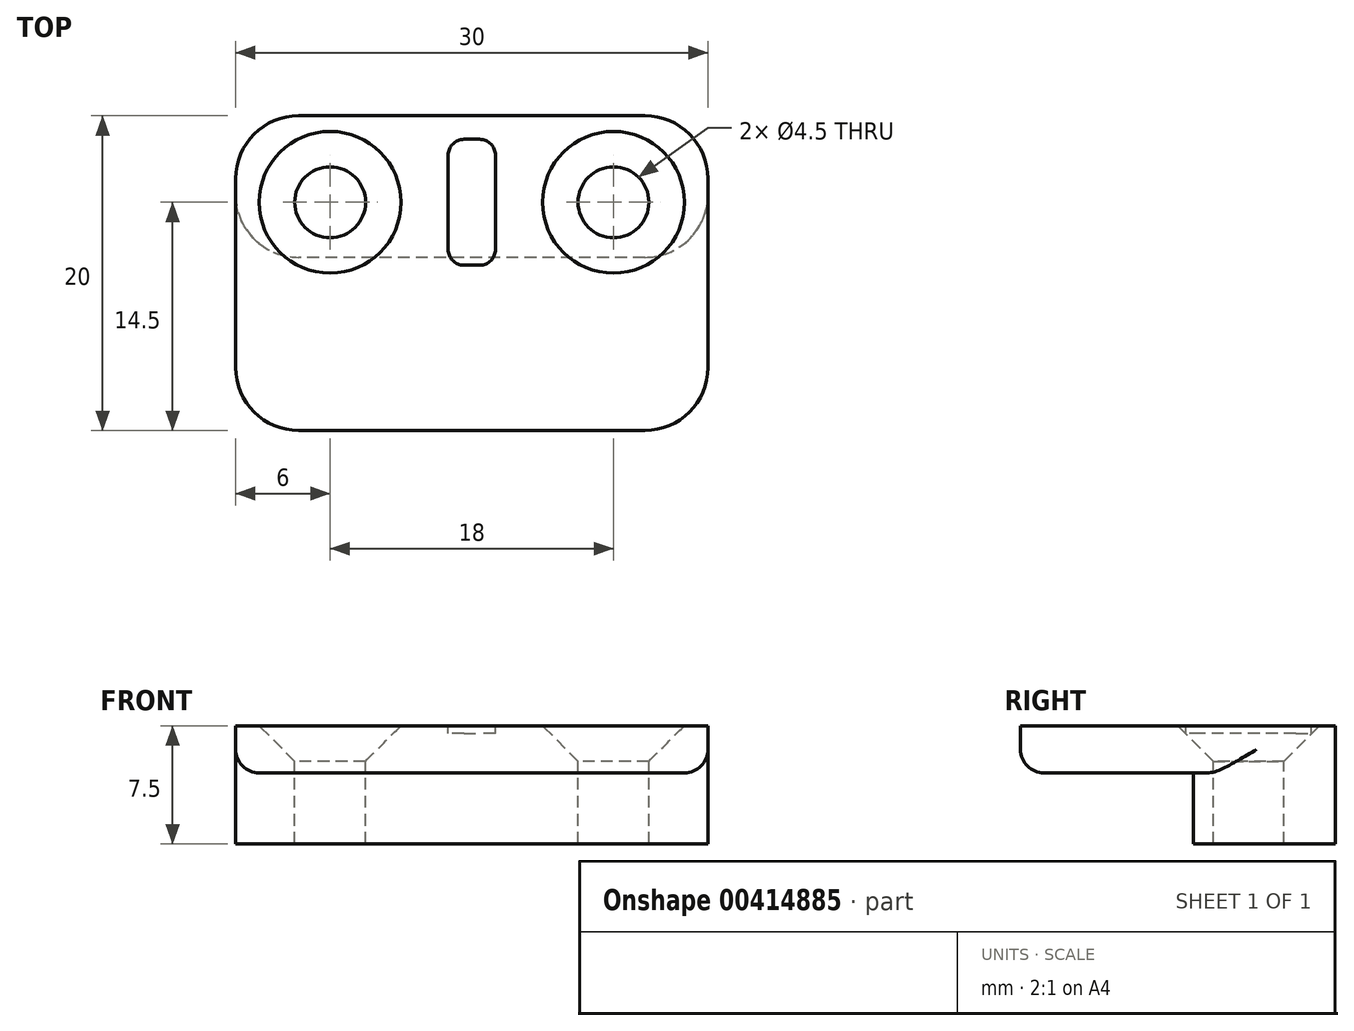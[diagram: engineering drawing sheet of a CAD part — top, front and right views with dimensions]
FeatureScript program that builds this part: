
annotation { "Feature Type Name" : "Feature", "Feature Type Description" : "" }
export const myFeature = defineFeature(function(context is Context, id is Id, definition is map)
    precondition{}
    {
        {
            var Q0;
            Q0=qCreatedBy(makeId("Right.planeOp"),FACE);
            var sketch = newSketch(context, id + "F0", { "sketchPlane" : qUnion([Q0])});
            skLineSegment(sketch, "E0", {"start": v(0, 0) * mm, "end": v(0, 4.5) * mm});
            skLineSegment(sketch, "E1", {"start": v(0, 4.5) * mm, "end": v(-11, 4.5) * mm});
            skLineSegment(sketch, "E2", {"start": v(-11, 4.5) * mm, "end": v(-11, 7.5) * mm});
            skLineSegment(sketch, "E3", {"start": v(-11, 7.5) * mm, "end": v(9, 7.5) * mm});
            skLineSegment(sketch, "E4", {"start": v(9, 7.5) * mm, "end": v(9, 0) * mm});
            skLineSegment(sketch, "E5", {"start": v(9, 0) * mm, "end": v(0, 0) * mm});
            skSolve(sketch);
        }
        {
            var Q0;
            Q0=makeQuery(id+"F0.imprint","IMPRINT",FACE,{"disambiguationData":[TD([[makeQuery(id+"F0.imprint","IMPRINT",EDGE,{"derivedFrom":sQuery(id+"F0.wireOp",EDGE,"E0")}),-1.0]])]});
            extrude(context, id + "F1", {"entities" : qUnion([Q0]), "endBound" : BoundingType.SYMMETRIC, "depth" : 30 * mm});
        }
        {
            var Q0;
            Q0=makeQuery(id+"F1.opExtrude","SWEPT_FACE",FACE,{"disambiguationData":[OSD([sQuery(id+"F0.wireOp",EDGE,"E3")])]});
            var sketch = newSketch(context, id + "F2", { "sketchPlane" : qUnion([Q0])});
            skLineSegment(sketch, "E6", {"start": v(-9, 3.5) * mm, "end": v(9, 3.5) * mm, "construction": true});
            skPoint(sketch, "E7.0", {"position": v(0, -11) * mm});
            skLineSegment(sketch, "E8", {"start": v(0, -11) * mm, "end": v(0, 3.5) * mm, "construction": true});
            skSolve(sketch);
        }
        {
            var Q0;
            Q0=sQuery(id+"F2.wireOp",VERTEX,"E6.start");
            var Q1;
            Q1=sQuery(id+"F2.wireOp",VERTEX,"E6.end");
            var Q2;
            Q2=makeQuery(id+"F1.opExtrude","SWEPT_BODY",BODY,{"disambiguationData":[OSD([sQuery(id+"F0.wireOp",EDGE,"E0"),sQuery(id+"F0.wireOp",EDGE,"E1"),sQuery(id+"F0.wireOp",EDGE,"E2"),sQuery(id+"F0.wireOp",EDGE,"E3"),sQuery(id+"F0.wireOp",EDGE,"E4"),sQuery(id+"F0.wireOp",EDGE,"E5")])]});
            hole(context, id + "F3", {"style" : HoleStyle.C_SINK, "endStyle" : HoleEndStyle.THROUGH, "holeDiameter" : 4.5 * mm, "cSinkDiameter" : 9 * mm, "cSinkAngle" : 90 * degree, "isTappedThrough" : true, "tappedDepth" : 12 * mm, "tapClearance" : 3, "locations" : qUnion([Q0, Q1]), "scope" : qUnion([Q2])});
        }
        {
            var Q0;
            Q0=makeQuery(id+"F1.opExtrude","CAP_EDGE",EDGE,{"disambiguationData":[OSD([sQuery(id+"F0.wireOp",EDGE,"E2")])],"isStart":false});
            var Q1;
            Q1=makeQuery(id+"F1.opExtrude","CAP_EDGE",EDGE,{"disambiguationData":[OSD([sQuery(id+"F0.wireOp",EDGE,"E2")])],"isStart":true});
            var Q2;
            Q2=makeQuery(id+"F1.opExtrude","CAP_EDGE",EDGE,{"disambiguationData":[OSD([sQuery(id+"F0.wireOp",EDGE,"E0")])],"isStart":false});
            var Q3;
            Q3=makeQuery(id+"F1.opExtrude","CAP_EDGE",EDGE,{"disambiguationData":[OSD([sQuery(id+"F0.wireOp",EDGE,"E0")])],"isStart":true});
            var Q4;
            Q4=makeQuery(id+"F1.opExtrude","CAP_EDGE",EDGE,{"disambiguationData":[OSD([sQuery(id+"F0.wireOp",EDGE,"E4")])],"isStart":true});
            var Q5;
            Q5=makeQuery(id+"F1.opExtrude","CAP_EDGE",EDGE,{"disambiguationData":[OSD([sQuery(id+"F0.wireOp",EDGE,"E4")])],"isStart":false});
            fillet(context, id + "F4", {"entities" : qUnion([Q0, Q1, Q2, Q3, Q4, Q5]), "radius" : 4 * mm, "tangentPropagation" : true, "allowEdgeOverflow" : false});
        }
        {
            var Q0;
            Q0=makeQuery(id+"F1.opExtrude","CAP_EDGE",EDGE,{"disambiguationData":[OSD([sQuery(id+"F0.wireOp",EDGE,"E1")])],"isStart":true});
            fillet(context, id + "F5", {"entities" : qUnion([Q0]), "radius" : 1.5 * mm, "tangentPropagation" : true, "allowEdgeOverflow" : false});
        }
        {
            var Q0;
            Q0=makeQuery(id+"F1.opExtrude","SWEPT_FACE",FACE,{"disambiguationData":[OSD([sQuery(id+"F0.wireOp",EDGE,"E3")])]});
            var sketch = newSketch(context, id + "F6", { "sketchPlane" : qUnion([Q0])});
            skLineSegment(sketch, "E9.bottom", {"start": v(-1.5, 7.5) * mm, "end": v(1.5, 7.5) * mm});
            skLineSegment(sketch, "E9.top", {"start": v(-1.5, -0.5) * mm, "end": v(1.5, -0.5) * mm});
            skLineSegment(sketch, "E9.left", {"start": v(-1.5, 7.5) * mm, "end": v(-1.5, -0.5) * mm});
            skLineSegment(sketch, "E9.right", {"start": v(1.5, 7.5) * mm, "end": v(1.5, -0.5) * mm});
            skPoint(sketch, "E10.0", {"position": v(0, 9) * mm});
            skLineSegment(sketch, "E11", {"start": v(0, 7.5) * mm, "end": v(0, -0.5) * mm, "construction": true});
            skSolve(sketch);
        }
        {
            var Q0;
            Q0=makeQuery(id+"F6.imprint","IMPRINT",FACE,{"disambiguationData":[TD([[makeQuery(id+"F6.imprint","IMPRINT",EDGE,{"derivedFrom":sQuery(id+"F6.wireOp",EDGE,"E9.bottom")}),-1.0]])]});
            extrude(context, id + "F7", {"entities" : qUnion([Q0]), "operationType" : NewBodyOperationType.REMOVE, "oppositeDirection" : true, "depth" : 0.5 * mm});
        }
        {
            var Q0;
            Q0=makeQuery(id+"F7.boolean.opBoolean","COPY",EDGE,{"derivedFrom":makeQuery(id+"F7.opExtrude","SWEPT_EDGE",EDGE,{"disambiguationData":[OSD([sQuery(id+"F6.wireOp",EDGE,"E9.bottom"),sQuery(id+"F6.wireOp",EDGE,"E9.left")])]})});
            var Q1;
            Q1=makeQuery(id+"F7.boolean.opBoolean","COPY",EDGE,{"derivedFrom":makeQuery(id+"F7.opExtrude","SWEPT_EDGE",EDGE,{"disambiguationData":[OSD([sQuery(id+"F6.wireOp",EDGE,"E9.top"),sQuery(id+"F6.wireOp",EDGE,"E9.left")])]})});
            var Q2;
            Q2=makeQuery(id+"F7.boolean.opBoolean","COPY",EDGE,{"derivedFrom":makeQuery(id+"F7.opExtrude","SWEPT_EDGE",EDGE,{"disambiguationData":[OSD([sQuery(id+"F6.wireOp",EDGE,"E9.top"),sQuery(id+"F6.wireOp",EDGE,"E9.right")])]})});
            var Q3;
            Q3=makeQuery(id+"F7.boolean.opBoolean","COPY",EDGE,{"derivedFrom":makeQuery(id+"F7.opExtrude","SWEPT_EDGE",EDGE,{"disambiguationData":[OSD([sQuery(id+"F6.wireOp",EDGE,"E9.bottom"),sQuery(id+"F6.wireOp",EDGE,"E9.right")])]})});
            fillet(context, id + "F8", {"entities" : qUnion([Q0, Q1, Q2, Q3]), "radius" : 1 * mm, "tangentPropagation" : true, "allowEdgeOverflow" : false});
        }
    });
